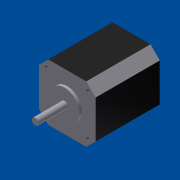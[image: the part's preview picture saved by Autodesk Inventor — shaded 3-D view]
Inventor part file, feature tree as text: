
AUTODESK INVENTOR PART (.ipt)
format: ipt  version: 2013 (Build 170138000, 138)  size: 135,680 bytes
history: native  units: in
note: dims shown in document units (in); Inventor stores cm internally (conversion verified against a paired STEP export)
features: sketch x5, extrude x4, hole x1, pattern_linear x1, chamfer x1
ambient origin geometry x8: Origin, YZ Plane, XZ Plane, XY Plane, X Axis, Y Axis, Z Axis, Center Point
bodies: Solid1 (feature_tree)
feature tree (12):
  extrude  "Extrusion1"  Depth=1.67in
  hole  "Hole1"  [1 undecoded]
  pattern_linear  "Rectangular Pattern1"  Count1=2 Spacing1=1.22in
  extrude  "Extrusion2"  Depth=0.7874in
  extrude  "Extrusion3"  Depth=0.87in
  chamfer  "Chamfer1"  Distance=0.0787in
  extrude  "Extrusion4"  Depth=0.1969in
  sketch  "Sketch1"  dims[d0=1.67in d1=1.67in]
  sketch  "Sketch2"  dims[d2=1.89in d3=0.0in d4=0.1181in]
  sketch  "Sketch3"  dims[d5=0.225in]
  sketch  "Sketch4"  dims[d6=0.225in]
  sketch  "Sketch5"  dims[d7=0.097in d8=0.1575in d9=0.375in d10=0.25in d11=0.5635in d12=0.1772in d13=0.8108in d14=0.7874in d16=1.22in d17=0.7874in d19=1.22in d20=0.87in d21=0.0787in d22=0.0in d23=0.1969in d24=0.8661in d25=0.0in d26=0.2756in d27=0.125in d28=45.0deg d29=0.1969in d30=0.835in d31=0.835in d32=0.3937in d33=0.0in]
note: 1 required parameter value undecoded (feature->parameter linkage not recoverable at this tier; creation-order binding heuristic only, values carry confidence <= 0.55)
